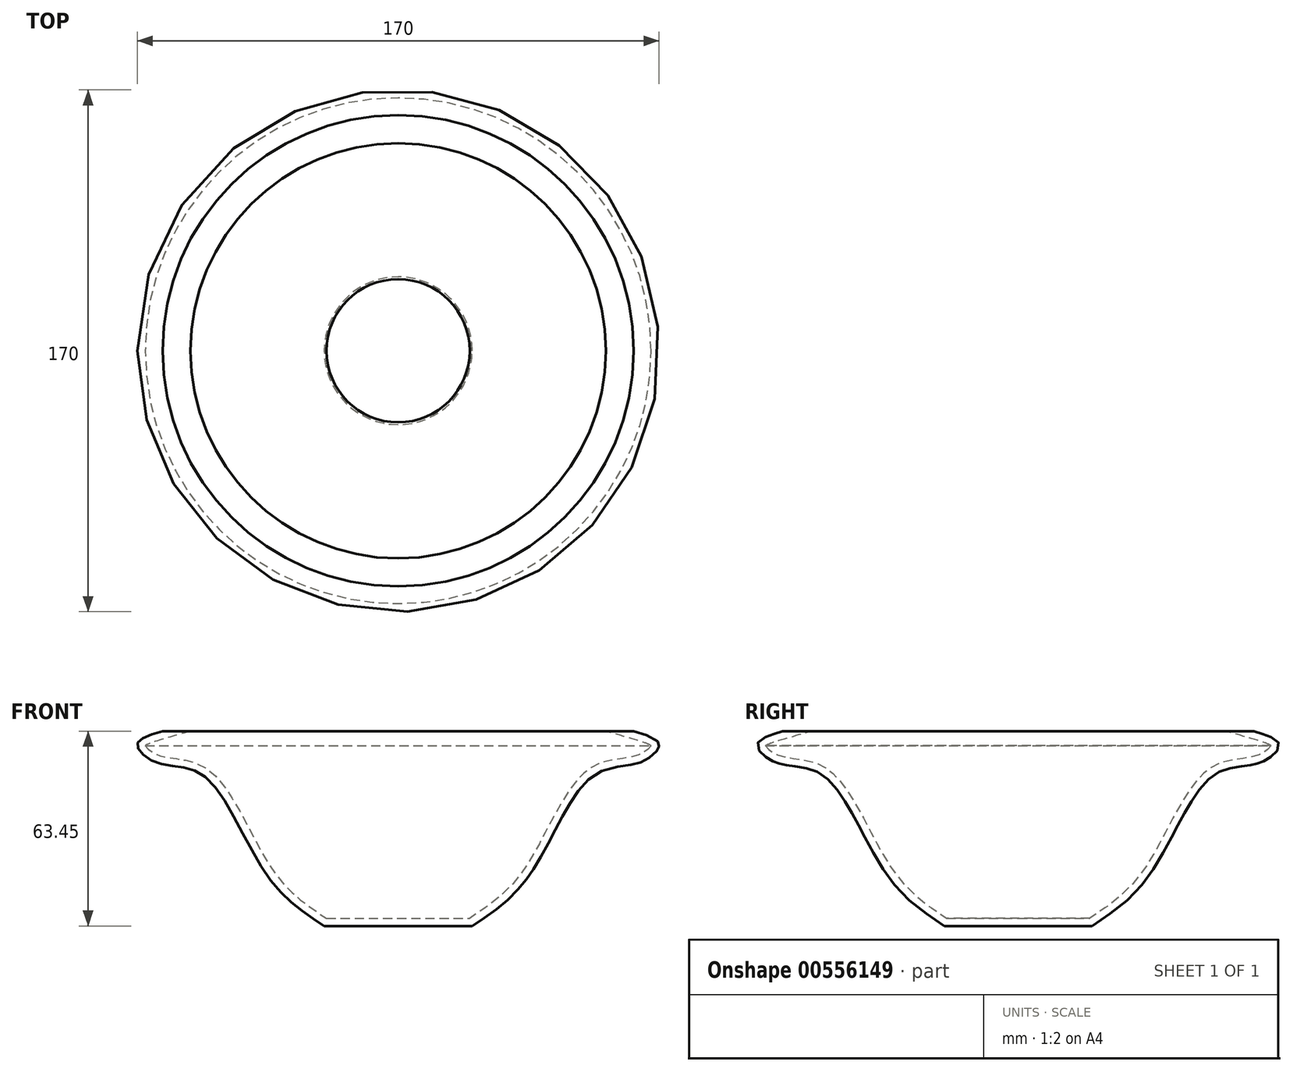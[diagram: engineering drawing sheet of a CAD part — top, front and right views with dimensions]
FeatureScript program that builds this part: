
annotation { "Feature Type Name" : "Feature", "Feature Type Description" : "" }
export const myFeature = defineFeature(function(context is Context, id is Id, definition is map)
    precondition{}
    {
        {
            var Q0;
            Q0=qCreatedBy(makeId("Front.planeOp"),FACE);
            var sketch = newSketch(context, id + "F0", { "sketchPlane" : qUnion([Q0])});
            skLineSegment(sketch, "E0", {"start": v(0, 67.7) * mm, "end": v(76.77, 67.7) * mm});
            skFitSpline(sketch, "E1", {"points": [v(76.77, 67.7) * mm, v(84.98, 63.45) * mm, v(78.75, 57.5) * mm, v(63.45, 53.26) * mm, v(43.06, 21.25) * mm, v(24.08, 4.25) * mm], "startDerivative": vector(82.3, -23.47) * mm, "endDerivative": vector(-83.12, -54.17) * mm});
            skLineSegment(sketch, "E2", {"start": v(24.08, 4.25) * mm, "end": v(0, 4.25) * mm});
            skLineSegment(sketch, "E3", {"start": v(0, 4.25) * mm, "end": v(0, 67.7) * mm});
            skSolve(sketch);
        }
        {
            var Q0;
            Q0 = qSketchRegion(id + "F0", true);
            var Q1;
            Q1=sQuery(id+"F0.wireOp",EDGE,"E3");
            revolve(context, id + "F1", {"entities" : qUnion([Q0]), "axis" : qUnion([Q1]), "revolveType" : RevolveType.FULL});
        }
        {
            var Q0;
            Q0=makeQuery(id+"F1.opRevolve","SWEPT_FACE",FACE,{"disambiguationData":[OSD([sQuery(id+"F0.wireOp",EDGE,"E0")])]});
            shell(context, id + "F2", {"entities" : qUnion([Q0]), "thickness" : 2.5 * mm});
        }
    });
